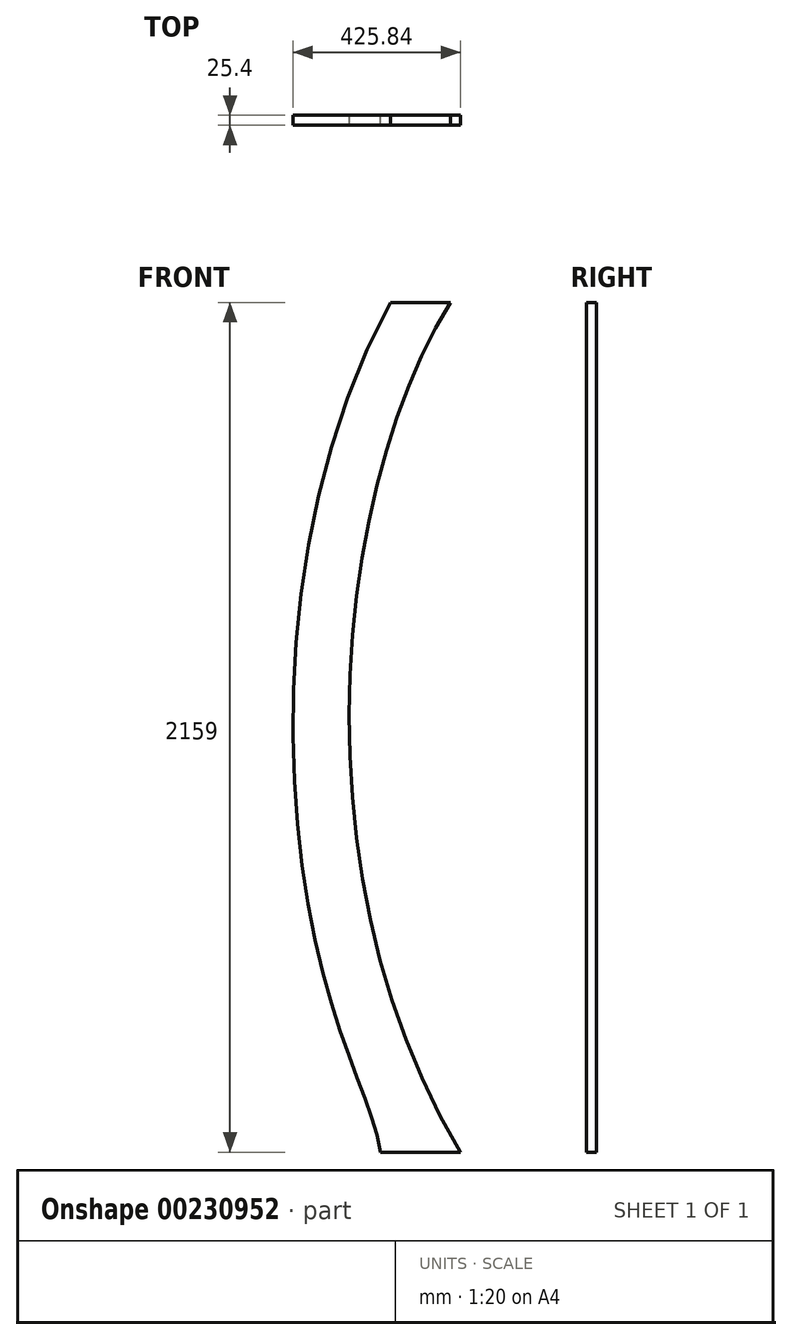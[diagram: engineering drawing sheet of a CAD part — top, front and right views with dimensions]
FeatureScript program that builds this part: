
annotation { "Feature Type Name" : "Feature", "Feature Type Description" : "" }
export const myFeature = defineFeature(function(context is Context, id is Id, definition is map)
    precondition{}
    {
        {
            var Q0;
            Q0=qCreatedBy(makeId("Front.planeOp"),FACE);
            var sketch = newSketch(context, id + "F0", { "sketchPlane" : qUnion([Q0])});
            skLineSegment(sketch, "E0", {"start": v(0, -1193.8) * mm, "end": v(-919.23, -1193.8) * mm});
            skLineSegment(sketch, "E1", {"start": v(0, 965.2) * mm, "end": v(-945.58, 965.2) * mm});
            skFitSpline(sketch, "E2", {"points": [v(-945.58, 965.2) * mm, v(-919.23, -1193.8) * mm], "startDerivative": vector(-889.45, -1441.33) * mm, "endDerivative": vector(1263.87, -2098.17) * mm});
            skLineSegment(sketch, "E3", {"start": v(-945.58, 965.2) * mm, "end": v(-1097.98, 965.2) * mm});
            skLineSegment(sketch, "E4", {"start": v(-919.23, -1193.8) * mm, "end": v(-1122.43, -1193.8) * mm});
            skFitSpline(sketch, "E5", {"points": [v(-1097.98, 965.2) * mm, v(-1266.7, -749.28) * mm, v(-1122.43, -1193.8) * mm], "startDerivative": vector(-1456.54, -2733.7) * mm, "endDerivative": vector(159.23, -982.95) * mm});
            skSolve(sketch);
        }
        {
            var Q0;
            Q0=qSketchRegion(id+"F0",true);
            extrude(context, id + "F1", {"entities" : qUnion([Q0]), "endBound" : BoundingType.SYMMETRIC, "depth" : 25.4 * mm});
        }
    });
